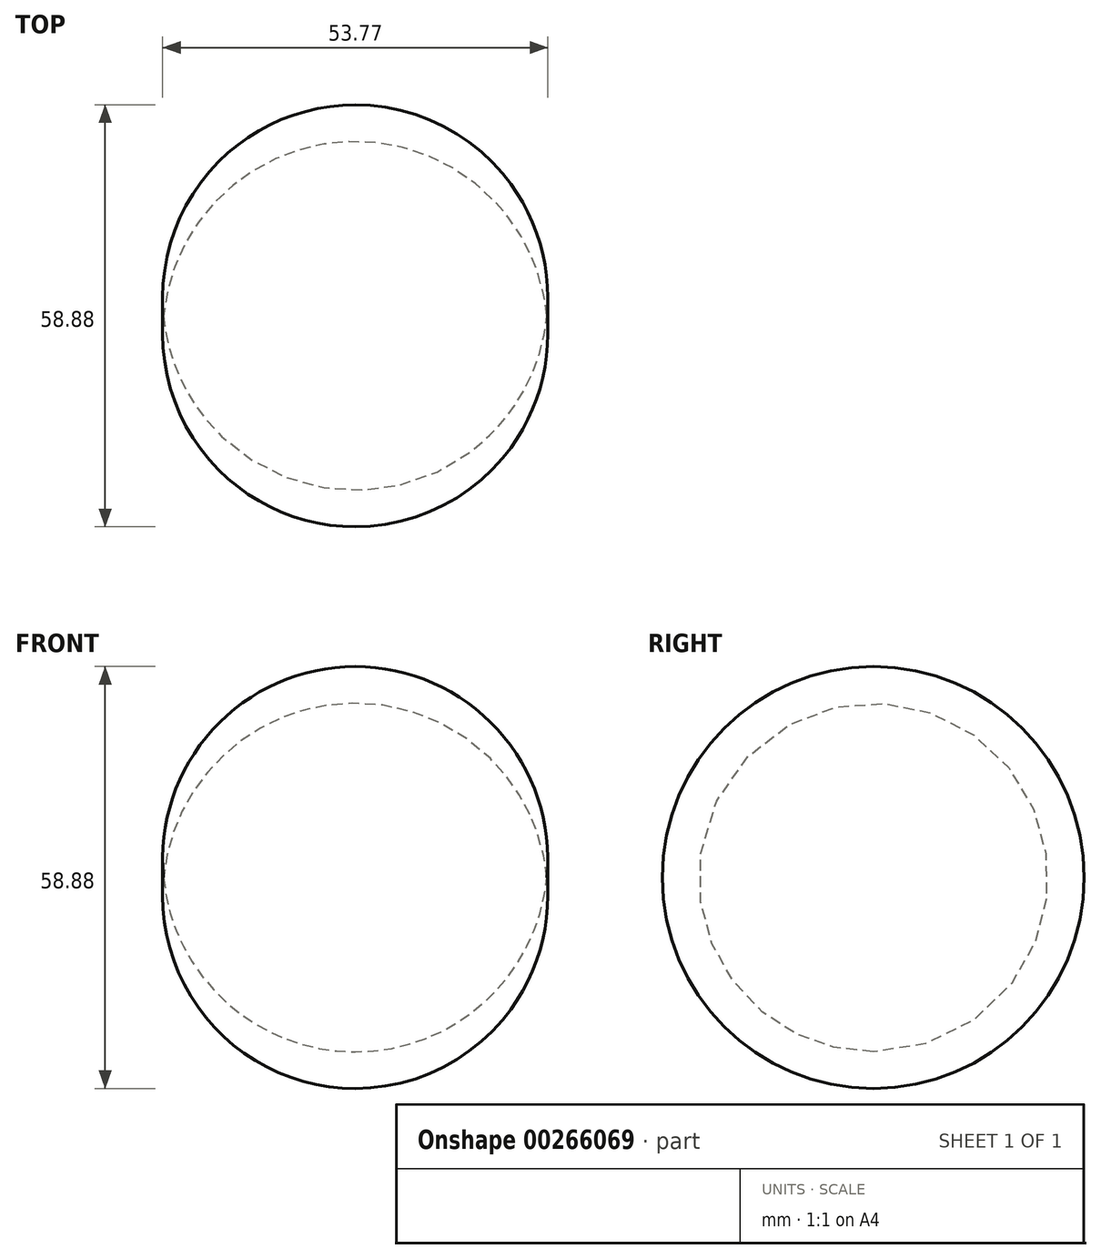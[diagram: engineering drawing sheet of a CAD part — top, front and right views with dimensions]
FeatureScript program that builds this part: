
annotation { "Feature Type Name" : "Feature", "Feature Type Description" : "" }
export const myFeature = defineFeature(function(context is Context, id is Id, definition is map)
    precondition{}
    {
        {
            var Q0;
            Q0=qCreatedBy(makeId("Front.planeOp"),FACE);
            var sketch = newSketch(context, id + "F0", { "sketchPlane" : qUnion([Q0])});
            skArc(sketch, "E0", {"start": v(27.79, 0) * mm, "mid": v(1.03, 24.33) * mm, "end": v(-25.74, 0) * mm});
            skLineSegment(sketch, "E1", {"start": v(-25.74, 0) * mm, "end": v(27.79, 0) * mm});
            skSolve(sketch);
        }
        {
            var Q0;
            Q0 = qSketchRegion(id + "F0", true);
            var Q1;
            Q1=sQuery(id+"F0.wireOp",EDGE,"E1");
            revolve(context, id + "F1", {"entities" : qUnion([Q0]), "axis" : qUnion([Q1]), "revolveType" : RevolveType.FULL});
        }
    });
